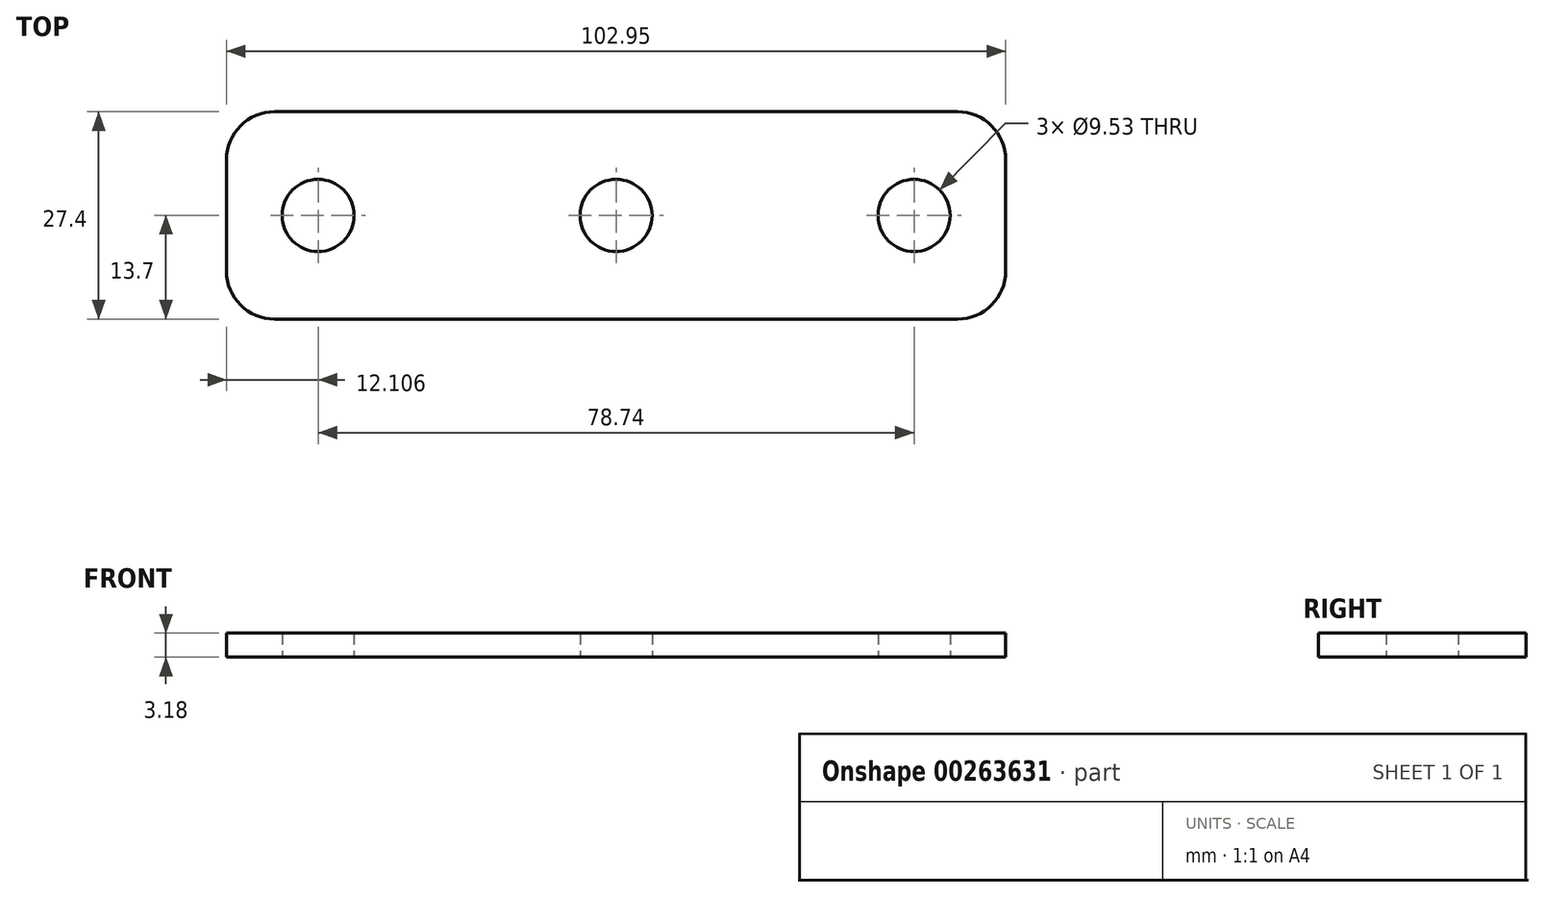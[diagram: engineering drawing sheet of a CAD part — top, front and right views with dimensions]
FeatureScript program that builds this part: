
annotation { "Feature Type Name" : "Feature", "Feature Type Description" : "" }
export const myFeature = defineFeature(function(context is Context, id is Id, definition is map)
    precondition{}
    {
        {
            var Q0;
            Q0=qCreatedBy(makeId("Top.planeOp"),FACE);
            var sketch = newSketch(context, id + "F0", { "sketchPlane" : qUnion([Q0])});
            skCircle(sketch, "E0", {"center": v(-17.13, 0) * mm, "radius": 4.76 * mm});
            skCircle(sketch, "E1", {"center": v(22.24, 0) * mm, "radius": 4.76 * mm});
            skPoint(sketch, "E2.middle", {"position": v(2.1, 0) * mm});
            skPoint(sketch, "E3.visualSharp", {"position": v(42.02, 19.57) * mm});
            skPoint(sketch, "E4.visualSharp", {"position": v(42.02, -5.76) * mm});
            skCircle(sketch, "E5", {"center": v(61.6, 0) * mm, "radius": 4.76 * mm});
            skLineSegment(sketch, "E6.bottom", {"start": v(67.36, 13.7) * mm, "end": v(-22.9, 13.7) * mm});
            skLineSegment(sketch, "E6.top", {"start": v(67.36, -13.7) * mm, "end": v(-22.9, -13.7) * mm});
            skLineSegment(sketch, "E6.left", {"start": v(73.71, 7.35) * mm, "end": v(73.71, -7.35) * mm});
            skLineSegment(sketch, "E6.right", {"start": v(-29.24, 7.35) * mm, "end": v(-29.24, -7.35) * mm});
            skPoint(sketch, "E7.visualSharp", {"position": v(-29.24, 13.7) * mm});
            skArc(sketch, "E7.filletArc", {"start": v(-22.9, 13.7) * mm, "mid": v(-27.38, 11.84) * mm, "end": v(-29.24, 7.35) * mm});
            skPoint(sketch, "E8.visualSharp", {"position": v(-29.24, -13.7) * mm});
            skArc(sketch, "E8.filletArc", {"start": v(-29.24, -7.35) * mm, "mid": v(-27.38, -11.84) * mm, "end": v(-22.9, -13.7) * mm});
            skPoint(sketch, "E9.visualSharp", {"position": v(73.71, -13.7) * mm});
            skArc(sketch, "E9.filletArc", {"start": v(67.36, -13.7) * mm, "mid": v(71.85, -11.84) * mm, "end": v(73.71, -7.35) * mm});
            skPoint(sketch, "E10.visualSharp", {"position": v(73.71, 13.7) * mm});
            skArc(sketch, "E10.filletArc", {"start": v(73.71, 7.35) * mm, "mid": v(71.85, 11.84) * mm, "end": v(67.36, 13.7) * mm});
            skSolve(sketch);
        }
        {
            var Q0;
            Q0=makeQuery(id+"F0.imprint","IMPRINT",FACE,{"disambiguationData":[TD([[makeQuery(id+"F0.imprint","IMPRINT",EDGE,{"derivedFrom":sQuery(id+"F0.wireOp",EDGE,"E0")}),-1.0]])]});
            extrude(context, id + "F1", {"entities" : qUnion([Q0]), "depth" : 3.17 * mm});
        }
    });
